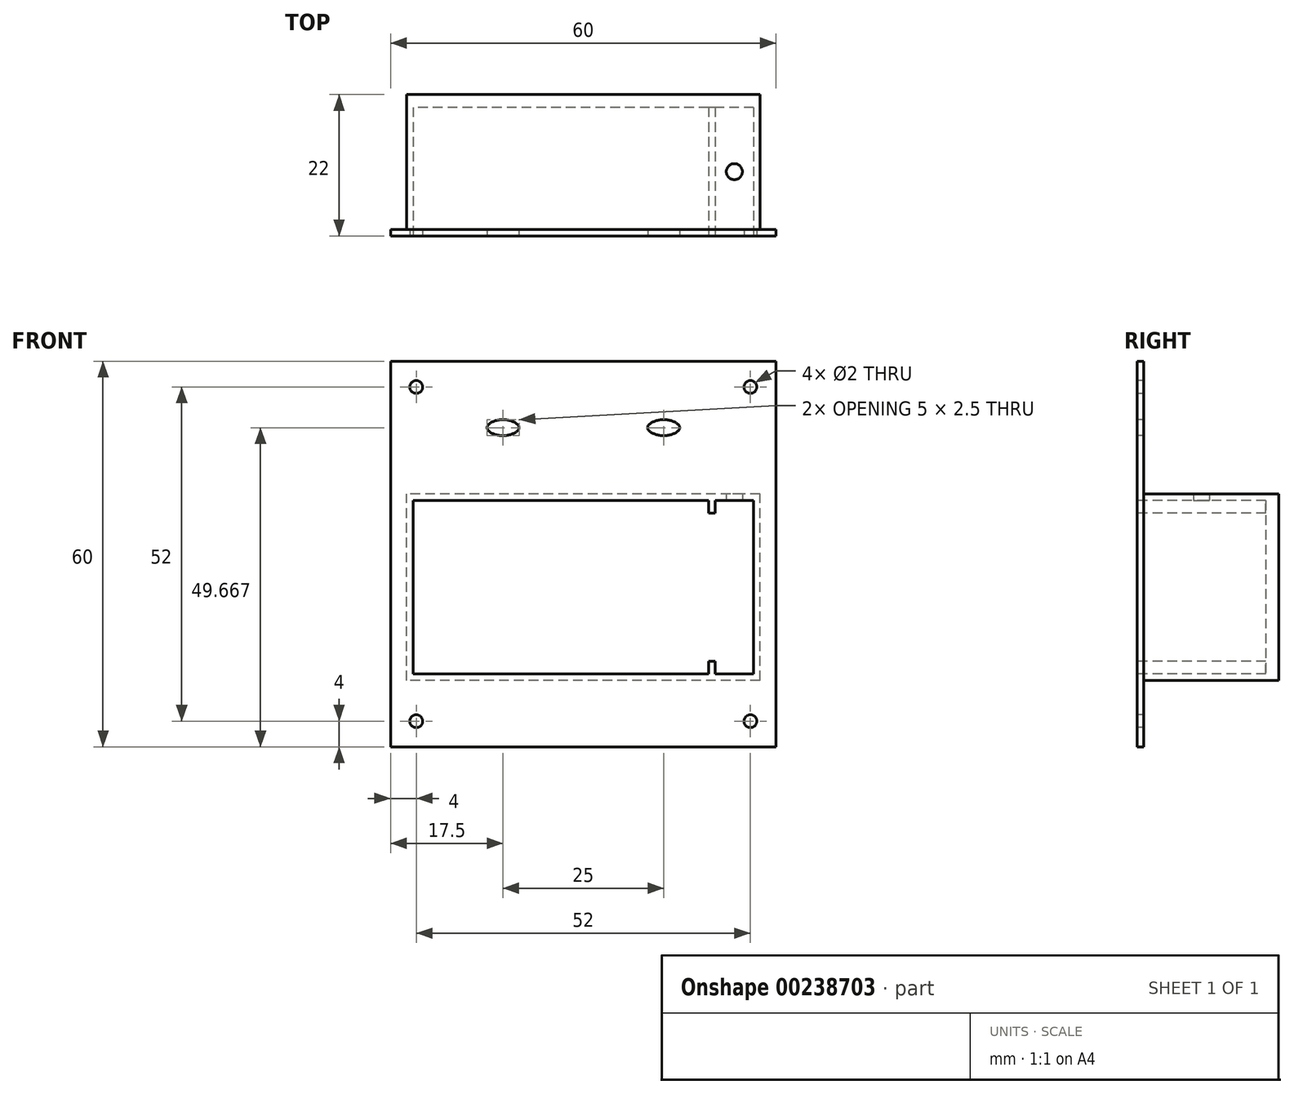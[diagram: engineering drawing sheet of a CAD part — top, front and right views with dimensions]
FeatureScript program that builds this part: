
annotation { "Feature Type Name" : "Feature", "Feature Type Description" : "" }
export const myFeature = defineFeature(function(context is Context, id is Id, definition is map)
    precondition{}
    {
        {
            var Q0;
            Q0=qCreatedBy(makeId("Front.planeOp"),FACE);
            var sketch = newSketch(context, id + "F0", { "sketchPlane" : qUnion([Q0])});
            skCircle(sketch, "E0", {"center": v(26.5, 16.25) * mm, "radius": 6.5 * mm, "construction": true});
            skCircle(sketch, "E1", {"center": v(45.5, 9.5) * mm, "radius": 4.5 * mm});
            skCircle(sketch, "E2", {"center": v(45.5, 9.5) * mm, "radius": 3 * mm});
            skCircle(sketch, "E3", {"center": v(45.5, 24.5) * mm, "radius": 3 * mm});
            skCircle(sketch, "E4", {"center": v(45.5, 24.5) * mm, "radius": 2.5 * mm});
            skLineSegment(sketch, "E5", {"start": v(45.5, 27.5) * mm, "end": v(45.5, 5) * mm, "construction": true});
            skPoint(sketch, "E6.positionSnap0", {"position": v(45.5, 16.25) * mm});
            skLineSegment(sketch, "E7.bottom", {"start": v(15, 32.5) * mm, "end": v(55, 32.5) * mm});
            skLineSegment(sketch, "E7.top", {"start": v(15, 0) * mm, "end": v(55, 0) * mm});
            skLineSegment(sketch, "E7.left", {"start": v(15, 32.5) * mm, "end": v(15, 0) * mm});
            skLineSegment(sketch, "E7.right", {"start": v(55, 32.5) * mm, "end": v(55, 0) * mm});
            skLineSegment(sketch, "E8", {"start": v(20.5, 22.25) * mm, "end": v(20.5, 23.75) * mm});
            skLineSegment(sketch, "E9", {"start": v(20.5, 23.75) * mm, "end": v(32.5, 23.75) * mm});
            skLineSegment(sketch, "E10", {"start": v(32.5, 23.75) * mm, "end": v(32.5, 22.25) * mm});
            skLineSegment(sketch, "E11", {"start": v(15, 16.25) * mm, "end": v(55, 16.25) * mm, "construction": true});
            skLineSegment(sketch, "E12.MirrorCS", {"start": v(32.5, 8.75) * mm, "end": v(32.5, 10.25) * mm});
            skLineSegment(sketch, "E13.MirrorCS", {"start": v(20.5, 8.75) * mm, "end": v(32.5, 8.75) * mm});
            skLineSegment(sketch, "E14.MirrorCS", {"start": v(20.5, 10.25) * mm, "end": v(20.5, 8.75) * mm});
            skLineSegment(sketch, "E15", {"start": v(50, 9.5) * mm, "end": v(55, 9.5) * mm, "construction": true});
            skLineSegment(sketch, "E16", {"start": v(41, 9.5) * mm, "end": v(41, 16.25) * mm, "construction": true});
            skLineSegment(sketch, "E17.bottom", {"start": v(32.5, 22.25) * mm, "end": v(20.5, 22.25) * mm});
            skLineSegment(sketch, "E17.top", {"start": v(32.5, 10.25) * mm, "end": v(20.5, 10.25) * mm});
            skLineSegment(sketch, "E17.left", {"start": v(32.5, 22.25) * mm, "end": v(32.5, 10.25) * mm});
            skLineSegment(sketch, "E17.right", {"start": v(20.5, 22.25) * mm, "end": v(20.5, 10.25) * mm});
            skLineSegment(sketch, "E18.bottom", {"start": v(24.5, 18.25) * mm, "end": v(28.5, 18.25) * mm});
            skLineSegment(sketch, "E18.top", {"start": v(24.5, 14.25) * mm, "end": v(28.5, 14.25) * mm});
            skLineSegment(sketch, "E18.left", {"start": v(24.5, 18.25) * mm, "end": v(24.5, 14.25) * mm});
            skLineSegment(sketch, "E18.right", {"start": v(28.5, 18.25) * mm, "end": v(28.5, 14.25) * mm});
            skLineSegment(sketch, "E19.1.0.0", {"start": v(92.5, 22.25) * mm, "end": v(80.5, 22.25) * mm});
            skCircle(sketch, "E19.1.0.1", {"center": v(105.5, 24.5) * mm, "radius": 2.5 * mm});
            skCircle(sketch, "E19.1.0.3", {"center": v(86.5, 16.25) * mm, "radius": 6.5 * mm, "construction": true});
            skLineSegment(sketch, "E19.1.0.4", {"start": v(115, 32.5) * mm, "end": v(115, 0) * mm});
            skLineSegment(sketch, "E19.1.0.5", {"start": v(75, 32.5) * mm, "end": v(115, 32.5) * mm});
            skLineSegment(sketch, "E19.1.0.6", {"start": v(84.5, 18.25) * mm, "end": v(84.5, 14.25) * mm});
            skLineSegment(sketch, "E19.1.0.7", {"start": v(84.5, 18.25) * mm, "end": v(88.5, 18.25) * mm});
            skLineSegment(sketch, "E19.1.0.8", {"start": v(92.5, 10.25) * mm, "end": v(80.5, 10.25) * mm});
            skLineSegment(sketch, "E19.1.0.9", {"start": v(80.5, 23.75) * mm, "end": v(92.5, 23.75) * mm});
            skCircle(sketch, "E19.1.0.10", {"center": v(105.5, 9.5) * mm, "radius": 4.5 * mm});
            skLineSegment(sketch, "E19.1.0.11", {"start": v(88.5, 18.25) * mm, "end": v(88.5, 14.25) * mm});
            skPoint(sketch, "E19.1.0.13", {"position": v(86.5, 16.25) * mm});
            skLineSegment(sketch, "E19.1.0.14", {"start": v(75, 32.5) * mm, "end": v(75, 0) * mm});
            skLineSegment(sketch, "E19.1.0.15", {"start": v(80.5, 8.75) * mm, "end": v(92.5, 8.75) * mm});
            skCircle(sketch, "E19.1.0.16", {"center": v(105.5, 9.5) * mm, "radius": 3 * mm});
            skCircle(sketch, "E19.1.0.17", {"center": v(105.5, 24.5) * mm, "radius": 3 * mm});
            skLineSegment(sketch, "E19.1.0.18", {"start": v(80.5, 22.25) * mm, "end": v(80.5, 10.25) * mm});
            skLineSegment(sketch, "E19.1.0.19", {"start": v(92.5, 22.25) * mm, "end": v(92.5, 10.25) * mm});
            skLineSegment(sketch, "E19.1.0.20", {"start": v(75, 0) * mm, "end": v(115, 0) * mm});
            skLineSegment(sketch, "E19.1.0.22", {"start": v(84.5, 14.25) * mm, "end": v(88.5, 14.25) * mm});
            skPoint(sketch, "E19.1.0.23", {"position": v(86.5, 16.25) * mm});
            skLineSegment(sketch, "E19.1.0.24", {"start": v(92.5, 23.75) * mm, "end": v(92.5, 22.25) * mm});
            skLineSegment(sketch, "E19.1.0.25", {"start": v(80.5, 22.25) * mm, "end": v(80.5, 23.75) * mm});
            skLineSegment(sketch, "E19.1.0.26", {"start": v(80.5, 10.25) * mm, "end": v(80.5, 8.75) * mm});
            skLineSegment(sketch, "E19.1.0.27", {"start": v(92.5, 8.75) * mm, "end": v(92.5, 10.25) * mm});
            skLineSegment(sketch, "E19.2.0.0", {"start": v(152.5, 22.25) * mm, "end": v(140.5, 22.25) * mm});
            skCircle(sketch, "E19.2.0.1", {"center": v(165.5, 24.5) * mm, "radius": 2.5 * mm});
            skCircle(sketch, "E19.2.0.3", {"center": v(146.5, 16.25) * mm, "radius": 6.5 * mm, "construction": true});
            skLineSegment(sketch, "E19.2.0.4", {"start": v(175, 32.5) * mm, "end": v(175, 0) * mm});
            skLineSegment(sketch, "E19.2.0.5", {"start": v(135, 32.5) * mm, "end": v(175, 32.5) * mm});
            skLineSegment(sketch, "E19.2.0.6", {"start": v(144.5, 18.25) * mm, "end": v(144.5, 14.25) * mm});
            skLineSegment(sketch, "E19.2.0.7", {"start": v(144.5, 18.25) * mm, "end": v(148.5, 18.25) * mm});
            skLineSegment(sketch, "E19.2.0.8", {"start": v(152.5, 10.25) * mm, "end": v(140.5, 10.25) * mm});
            skLineSegment(sketch, "E19.2.0.9", {"start": v(140.5, 23.75) * mm, "end": v(152.5, 23.75) * mm});
            skCircle(sketch, "E19.2.0.10", {"center": v(165.5, 9.5) * mm, "radius": 4.5 * mm});
            skLineSegment(sketch, "E19.2.0.11", {"start": v(148.5, 18.25) * mm, "end": v(148.5, 14.25) * mm});
            skPoint(sketch, "E19.2.0.13", {"position": v(146.5, 16.25) * mm});
            skLineSegment(sketch, "E19.2.0.14", {"start": v(135, 32.5) * mm, "end": v(135, 0) * mm});
            skLineSegment(sketch, "E19.2.0.15", {"start": v(140.5, 8.75) * mm, "end": v(152.5, 8.75) * mm});
            skCircle(sketch, "E19.2.0.16", {"center": v(165.5, 9.5) * mm, "radius": 3 * mm});
            skCircle(sketch, "E19.2.0.17", {"center": v(165.5, 24.5) * mm, "radius": 3 * mm});
            skLineSegment(sketch, "E19.2.0.18", {"start": v(140.5, 22.25) * mm, "end": v(140.5, 10.25) * mm});
            skLineSegment(sketch, "E19.2.0.19", {"start": v(152.5, 22.25) * mm, "end": v(152.5, 10.25) * mm});
            skLineSegment(sketch, "E19.2.0.20", {"start": v(135, 0) * mm, "end": v(175, 0) * mm});
            skLineSegment(sketch, "E19.2.0.22", {"start": v(144.5, 14.25) * mm, "end": v(148.5, 14.25) * mm});
            skPoint(sketch, "E19.2.0.23", {"position": v(146.5, 16.25) * mm});
            skLineSegment(sketch, "E19.2.0.24", {"start": v(152.5, 23.75) * mm, "end": v(152.5, 22.25) * mm});
            skLineSegment(sketch, "E19.2.0.25", {"start": v(140.5, 22.25) * mm, "end": v(140.5, 23.75) * mm});
            skLineSegment(sketch, "E19.2.0.26", {"start": v(140.5, 10.25) * mm, "end": v(140.5, 8.75) * mm});
            skLineSegment(sketch, "E19.2.0.27", {"start": v(152.5, 8.75) * mm, "end": v(152.5, 10.25) * mm});
            skLineSegment(sketch, "E19.3.0.0", {"start": v(212.5, 22.25) * mm, "end": v(200.5, 22.25) * mm});
            skCircle(sketch, "E19.3.0.1", {"center": v(225.5, 24.5) * mm, "radius": 2.5 * mm});
            skCircle(sketch, "E19.3.0.3", {"center": v(206.5, 16.25) * mm, "radius": 6.5 * mm, "construction": true});
            skLineSegment(sketch, "E19.3.0.4", {"start": v(235, 32.5) * mm, "end": v(235, 0) * mm});
            skLineSegment(sketch, "E19.3.0.5", {"start": v(195, 32.5) * mm, "end": v(235, 32.5) * mm});
            skLineSegment(sketch, "E19.3.0.6", {"start": v(204.5, 18.25) * mm, "end": v(204.5, 14.25) * mm});
            skLineSegment(sketch, "E19.3.0.7", {"start": v(204.5, 18.25) * mm, "end": v(208.5, 18.25) * mm});
            skLineSegment(sketch, "E19.3.0.8", {"start": v(212.5, 10.25) * mm, "end": v(200.5, 10.25) * mm});
            skLineSegment(sketch, "E19.3.0.9", {"start": v(200.5, 23.75) * mm, "end": v(212.5, 23.75) * mm});
            skCircle(sketch, "E19.3.0.10", {"center": v(225.5, 9.5) * mm, "radius": 4.5 * mm});
            skLineSegment(sketch, "E19.3.0.11", {"start": v(208.5, 18.25) * mm, "end": v(208.5, 14.25) * mm});
            skPoint(sketch, "E19.3.0.13", {"position": v(206.5, 16.25) * mm});
            skLineSegment(sketch, "E19.3.0.14", {"start": v(195, 32.5) * mm, "end": v(195, 0) * mm});
            skLineSegment(sketch, "E19.3.0.15", {"start": v(200.5, 8.75) * mm, "end": v(212.5, 8.75) * mm});
            skCircle(sketch, "E19.3.0.16", {"center": v(225.5, 9.5) * mm, "radius": 3 * mm});
            skCircle(sketch, "E19.3.0.17", {"center": v(225.5, 24.5) * mm, "radius": 3 * mm});
            skLineSegment(sketch, "E19.3.0.18", {"start": v(200.5, 22.25) * mm, "end": v(200.5, 10.25) * mm});
            skLineSegment(sketch, "E19.3.0.19", {"start": v(212.5, 22.25) * mm, "end": v(212.5, 10.25) * mm});
            skLineSegment(sketch, "E19.3.0.20", {"start": v(195, 0) * mm, "end": v(235, 0) * mm});
            skLineSegment(sketch, "E19.3.0.22", {"start": v(204.5, 14.25) * mm, "end": v(208.5, 14.25) * mm});
            skPoint(sketch, "E19.3.0.23", {"position": v(206.5, 16.25) * mm});
            skLineSegment(sketch, "E19.3.0.24", {"start": v(212.5, 23.75) * mm, "end": v(212.5, 22.25) * mm});
            skLineSegment(sketch, "E19.3.0.25", {"start": v(200.5, 22.25) * mm, "end": v(200.5, 23.75) * mm});
            skLineSegment(sketch, "E19.3.0.26", {"start": v(200.5, 10.25) * mm, "end": v(200.5, 8.75) * mm});
            skLineSegment(sketch, "E19.3.0.27", {"start": v(212.5, 8.75) * mm, "end": v(212.5, 10.25) * mm});
            skLineSegment(sketch, "E19.direction1", {"start": v(15, 0) * mm, "end": v(75, 0) * mm, "construction": true});
            skLineSegment(sketch, "E20.bottom", {"start": v(0, -92.5) * mm, "end": v(250, -92.5) * mm, "construction": true});
            skLineSegment(sketch, "E20.top", {"start": v(0, 47.5) * mm, "end": v(250, 47.5) * mm, "construction": true});
            skLineSegment(sketch, "E20.right", {"start": v(250, -92.5) * mm, "end": v(250, 47.5) * mm, "construction": true});
            skLineSegment(sketch, "E21", {"start": v(115, 0) * mm, "end": v(135, 0) * mm, "construction": true});
            skLineSegment(sketch, "E22.bottom", {"start": v(144.5, -39.17) * mm, "end": v(98.5, -39.17) * mm});
            skLineSegment(sketch, "E22.top", {"start": v(144.5, -66.17) * mm, "end": v(98.5, -66.17) * mm});
            skLineSegment(sketch, "E22.right", {"start": v(98.5, -39.17) * mm, "end": v(98.5, -66.17) * mm});
            skLineSegment(sketch, "E23.bottom", {"start": v(151.5, -39.17) * mm, "end": v(145.5, -39.17) * mm});
            skLineSegment(sketch, "E23.top", {"start": v(151.5, -66.17) * mm, "end": v(145.5, -66.17) * mm});
            skLineSegment(sketch, "E23.left", {"start": v(151.5, -39.17) * mm, "end": v(151.5, -66.17) * mm});
            skLineSegment(sketch, "E24.bottom", {"start": v(152.5, -67.17) * mm, "end": v(97.5, -67.17) * mm});
            skLineSegment(sketch, "E24.top", {"start": v(152.5, -38.17) * mm, "end": v(97.5, -38.17) * mm});
            skLineSegment(sketch, "E24.left", {"start": v(152.5, -67.17) * mm, "end": v(152.5, -38.17) * mm});
            skLineSegment(sketch, "E24.right", {"start": v(97.5, -67.17) * mm, "end": v(97.5, -38.17) * mm});
            skLineSegment(sketch, "E25", {"start": v(145.5, -64.17) * mm, "end": v(144.5, -64.17) * mm});
            skLineSegment(sketch, "E26", {"start": v(145.5, -41.17) * mm, "end": v(144.5, -41.17) * mm});
            skLineSegment(sketch, "E27", {"start": v(145.5, -66.17) * mm, "end": v(145.5, -64.17) * mm});
            skLineSegment(sketch, "E28", {"start": v(144.5, -66.17) * mm, "end": v(144.5, -64.17) * mm});
            skLineSegment(sketch, "E29", {"start": v(145.5, -41.17) * mm, "end": v(145.5, -39.17) * mm});
            skLineSegment(sketch, "E30", {"start": v(144.5, -41.17) * mm, "end": v(144.5, -39.17) * mm});
            skLineSegment(sketch, "E31.bottom", {"start": v(95, -77.5) * mm, "end": v(95, -17.5) * mm});
            skLineSegment(sketch, "E31.top", {"start": v(155, -77.5) * mm, "end": v(155, -17.5) * mm});
            skLineSegment(sketch, "E31.left", {"start": v(95, -77.5) * mm, "end": v(155, -77.5) * mm});
            skLineSegment(sketch, "E31.right", {"start": v(95, -17.5) * mm, "end": v(155, -17.5) * mm});
            skLineSegment(sketch, "E32", {"start": v(125, -38.17) * mm, "end": v(125, -17.5) * mm, "construction": true});
            skLineSegment(sketch, "E33", {"start": v(97.5, -67.17) * mm, "end": v(97.5, -77.5) * mm, "construction": true});
            skLineSegment(sketch, "E34", {"start": v(125, 0) * mm, "end": v(125, -92.5) * mm, "construction": true});
            skLineSegment(sketch, "E35.1.0.0", {"start": v(175, -77.5) * mm, "end": v(175, -17.5) * mm});
            skLineSegment(sketch, "E35.1.0.1", {"start": v(235, -77.5) * mm, "end": v(235, -17.5) * mm});
            skLineSegment(sketch, "E35.1.0.2", {"start": v(232.5, -67.17) * mm, "end": v(177.5, -67.17) * mm});
            skLineSegment(sketch, "E35.1.0.3", {"start": v(232.5, -67.17) * mm, "end": v(232.5, -38.17) * mm});
            skLineSegment(sketch, "E35.1.0.4", {"start": v(175, -17.5) * mm, "end": v(235, -17.5) * mm});
            skLineSegment(sketch, "E35.1.0.5", {"start": v(178.5, -39.17) * mm, "end": v(178.5, -66.17) * mm});
            skLineSegment(sketch, "E35.1.0.9", {"start": v(224.5, -66.17) * mm, "end": v(178.5, -66.17) * mm});
            skLineSegment(sketch, "E35.1.0.10", {"start": v(205, -38.17) * mm, "end": v(205, -17.5) * mm, "construction": true});
            skLineSegment(sketch, "E35.1.0.11", {"start": v(177.5, -67.17) * mm, "end": v(177.5, -77.5) * mm, "construction": true});
            skLineSegment(sketch, "E35.1.0.12", {"start": v(232.5, -38.17) * mm, "end": v(177.5, -38.17) * mm});
            skLineSegment(sketch, "E35.1.0.14", {"start": v(224.5, -39.17) * mm, "end": v(178.5, -39.17) * mm});
            skLineSegment(sketch, "E35.1.0.17", {"start": v(175, -77.5) * mm, "end": v(235, -77.5) * mm});
            skLineSegment(sketch, "E35.1.0.18", {"start": v(231.5, -39.17) * mm, "end": v(231.5, -66.17) * mm});
            skLineSegment(sketch, "E35.1.0.19", {"start": v(177.5, -67.17) * mm, "end": v(177.5, -38.17) * mm});
            skLineSegment(sketch, "E35.1.0.23", {"start": v(224.5, -41.17) * mm, "end": v(224.5, -39.17) * mm});
            skLineSegment(sketch, "E35.1.0.24", {"start": v(231.5, -39.17) * mm, "end": v(225.5, -39.17) * mm});
            skLineSegment(sketch, "E35.1.0.25", {"start": v(225.5, -41.17) * mm, "end": v(225.5, -39.17) * mm});
            skLineSegment(sketch, "E35.1.0.26", {"start": v(231.5, -66.17) * mm, "end": v(225.5, -66.17) * mm});
            skLineSegment(sketch, "E35.1.0.27", {"start": v(225.5, -66.17) * mm, "end": v(225.5, -64.17) * mm});
            skLineSegment(sketch, "E35.1.0.28", {"start": v(225.5, -41.17) * mm, "end": v(224.5, -41.17) * mm});
            skLineSegment(sketch, "E35.1.0.29", {"start": v(224.5, -66.17) * mm, "end": v(224.5, -64.17) * mm});
            skLineSegment(sketch, "E35.1.0.30", {"start": v(225.5, -64.17) * mm, "end": v(224.5, -64.17) * mm});
            skLineSegment(sketch, "E35.direction1", {"start": v(95, -77.5) * mm, "end": v(175, -77.5) * mm, "construction": true});
            skLineSegment(sketch, "E36.bottom", {"start": v(36.67, -28) * mm, "end": v(36.67, -74) * mm});
            skLineSegment(sketch, "E36.top", {"start": v(63.67, -28) * mm, "end": v(63.67, -74) * mm});
            skLineSegment(sketch, "E36.right", {"start": v(36.67, -74) * mm, "end": v(63.67, -74) * mm});
            skLineSegment(sketch, "E37.bottom", {"start": v(36.67, -21) * mm, "end": v(36.67, -27) * mm});
            skLineSegment(sketch, "E37.top", {"start": v(63.67, -21) * mm, "end": v(63.67, -27) * mm});
            skLineSegment(sketch, "E37.left", {"start": v(36.67, -21) * mm, "end": v(63.67, -21) * mm});
            skLineSegment(sketch, "E38.bottom", {"start": v(64.67, -20) * mm, "end": v(64.67, -75) * mm});
            skLineSegment(sketch, "E38.top", {"start": v(35.67, -20) * mm, "end": v(35.67, -75) * mm});
            skLineSegment(sketch, "E38.left", {"start": v(64.67, -20) * mm, "end": v(35.67, -20) * mm});
            skLineSegment(sketch, "E38.right", {"start": v(64.67, -75) * mm, "end": v(35.67, -75) * mm});
            skLineSegment(sketch, "E39", {"start": v(61.67, -27) * mm, "end": v(61.67, -28) * mm});
            skLineSegment(sketch, "E40", {"start": v(38.67, -27) * mm, "end": v(38.67, -28) * mm});
            skLineSegment(sketch, "E41", {"start": v(63.67, -27) * mm, "end": v(61.67, -27) * mm});
            skLineSegment(sketch, "E42", {"start": v(63.67, -28) * mm, "end": v(61.67, -28) * mm});
            skLineSegment(sketch, "E43", {"start": v(38.67, -27) * mm, "end": v(36.67, -27) * mm});
            skLineSegment(sketch, "E44", {"start": v(38.67, -28) * mm, "end": v(36.67, -28) * mm});
            skLineSegment(sketch, "E45.bottom", {"start": v(75, -77.5) * mm, "end": v(15, -77.5) * mm});
            skLineSegment(sketch, "E45.top", {"start": v(75, -17.5) * mm, "end": v(15, -17.5) * mm});
            skLineSegment(sketch, "E45.left", {"start": v(75, -77.5) * mm, "end": v(75, -17.5) * mm});
            skLineSegment(sketch, "E45.right", {"start": v(15, -77.5) * mm, "end": v(15, -17.5) * mm});
            skLineSegment(sketch, "E46", {"start": v(25.33, -29.08) * mm, "end": v(15, -29.08) * mm, "construction": true});
            skLineSegment(sketch, "E47", {"start": v(64.67, -29.08) * mm, "end": v(75, -29.08) * mm, "construction": true});
            skLineSegment(sketch, "E48", {"start": v(25.33, -29.08) * mm, "end": v(35.67, -29.08) * mm, "construction": true});
            skCircle(sketch, "E49", {"center": v(19, 28.5) * mm, "radius": 1 * mm});
            skCircle(sketch, "E50", {"center": v(51, 28.5) * mm, "radius": 1 * mm});
            skCircle(sketch, "E51", {"center": v(51, 4) * mm, "radius": 1 * mm});
            skCircle(sketch, "E52", {"center": v(19, 4) * mm, "radius": 1 * mm});
            skCircle(sketch, "E53", {"center": v(19, -21.5) * mm, "radius": 1 * mm});
            skCircle(sketch, "E54", {"center": v(71, -21.5) * mm, "radius": 1 * mm});
            skCircle(sketch, "E55", {"center": v(19, -73.5) * mm, "radius": 1 * mm});
            skCircle(sketch, "E56", {"center": v(71, -73.5) * mm, "radius": 1 * mm});
            skCircle(sketch, "E57.1.0.0", {"center": v(79, 28.5) * mm, "radius": 1 * mm});
            skCircle(sketch, "E57.1.0.1", {"center": v(79, 4) * mm, "radius": 1 * mm});
            skCircle(sketch, "E57.1.0.2", {"center": v(111, 4) * mm, "radius": 1 * mm});
            skCircle(sketch, "E57.1.0.3", {"center": v(111, 28.5) * mm, "radius": 1 * mm});
            skCircle(sketch, "E57.2.0.0", {"center": v(139, 28.5) * mm, "radius": 1 * mm});
            skCircle(sketch, "E57.2.0.1", {"center": v(139, 4) * mm, "radius": 1 * mm});
            skCircle(sketch, "E57.2.0.2", {"center": v(171, 4) * mm, "radius": 1 * mm});
            skCircle(sketch, "E57.2.0.3", {"center": v(171, 28.5) * mm, "radius": 1 * mm});
            skCircle(sketch, "E57.3.0.0", {"center": v(199, 28.5) * mm, "radius": 1 * mm});
            skCircle(sketch, "E57.3.0.1", {"center": v(199, 4) * mm, "radius": 1 * mm});
            skCircle(sketch, "E57.3.0.2", {"center": v(231, 4) * mm, "radius": 1 * mm});
            skCircle(sketch, "E57.3.0.3", {"center": v(231, 28.5) * mm, "radius": 1 * mm});
            skLineSegment(sketch, "E57.direction1", {"start": v(19, 4) * mm, "end": v(79, 4) * mm, "construction": true});
            skCircle(sketch, "E58.1.0.0", {"center": v(99, -73.5) * mm, "radius": 1 * mm});
            skCircle(sketch, "E58.1.0.1", {"center": v(151, -73.5) * mm, "radius": 1 * mm});
            skCircle(sketch, "E58.1.0.2", {"center": v(151, -21.5) * mm, "radius": 1 * mm});
            skCircle(sketch, "E58.1.0.3", {"center": v(99, -21.5) * mm, "radius": 1 * mm});
            skCircle(sketch, "E58.2.0.0", {"center": v(179, -73.5) * mm, "radius": 1 * mm});
            skCircle(sketch, "E58.2.0.1", {"center": v(231, -73.5) * mm, "radius": 1 * mm});
            skCircle(sketch, "E58.2.0.2", {"center": v(231, -21.5) * mm, "radius": 1 * mm});
            skCircle(sketch, "E58.2.0.3", {"center": v(179, -21.5) * mm, "radius": 1 * mm});
            skLineSegment(sketch, "E58.direction1", {"start": v(19, -73.5) * mm, "end": v(99, -73.5) * mm, "construction": true});
            skPoint(sketch, "E59.middle", {"position": v(25.33, -27.83) * mm});
            skLineSegment(sketch, "E60", {"start": v(15, -47.5) * mm, "end": v(35.67, -47.5) * mm, "construction": true});
            skPoint(sketch, "E61.1.0.0", {"position": v(112.5, -27.83) * mm});
            skLineSegment(sketch, "E62", {"start": v(112.5, -26.58) * mm, "end": v(112.5, -27.83) * mm, "construction": true});
            skLineSegment(sketch, "E63.bottom", {"start": v(115, -29.08) * mm, "end": v(110, -29.08) * mm, "construction": true});
            skLineSegment(sketch, "E63.top", {"start": v(115, -26.58) * mm, "end": v(110, -26.58) * mm, "construction": true});
            skLineSegment(sketch, "E63.left", {"start": v(115, -29.08) * mm, "end": v(115, -26.58) * mm, "construction": true});
            skLineSegment(sketch, "E63.right", {"start": v(110, -29.08) * mm, "end": v(110, -26.58) * mm, "construction": true});
            skFitSpline(sketch, "E64", {"points": [v(110, -27.83) * mm, v(110.5, -27.13) * mm, v(112.5, -26.58) * mm], "startDerivative": vector(0, 1.91) * mm, "endDerivative": vector(3.95, 0) * mm});
            skLineSegment(sketch, "E65", {"start": v(110, -27.83) * mm, "end": v(112.5, -27.83) * mm, "construction": true});
            skFitSpline(sketch, "E66.MirrorCS", {"points": [v(115, -27.83) * mm, v(114.5, -27.13) * mm, v(112.5, -26.58) * mm], "startDerivative": vector(0, 1.91) * mm, "endDerivative": vector(-3.95, 0) * mm});
            skFitSpline(sketch, "E67.MirrorCS", {"points": [v(110, -27.83) * mm, v(110.5, -28.53) * mm, v(112.5, -29.08) * mm], "startDerivative": vector(0, -1.91) * mm, "endDerivative": vector(3.95, 0) * mm});
            skFitSpline(sketch, "E68.MirrorCS", {"points": [v(115, -27.83) * mm, v(114.5, -28.53) * mm, v(112.5, -29.08) * mm], "startDerivative": vector(0, -1.91) * mm, "endDerivative": vector(-3.95, 0) * mm});
            skLineSegment(sketch, "E69", {"start": v(25.33, -17.5) * mm, "end": v(25.33, -27.83) * mm, "construction": true});
            skLineSegment(sketch, "E70.bottom", {"start": v(27.83, -29.08) * mm, "end": v(22.83, -29.08) * mm, "construction": true});
            skLineSegment(sketch, "E70.top", {"start": v(27.83, -26.58) * mm, "end": v(22.83, -26.58) * mm, "construction": true});
            skLineSegment(sketch, "E70.left", {"start": v(27.83, -29.08) * mm, "end": v(27.83, -26.58) * mm, "construction": true});
            skLineSegment(sketch, "E70.right", {"start": v(22.83, -29.08) * mm, "end": v(22.83, -26.58) * mm, "construction": true});
            skFitSpline(sketch, "E71", {"points": [v(22.83, -27.83) * mm, v(23.33, -27.13) * mm, v(25.33, -26.58) * mm], "startDerivative": vector(0, 1.91) * mm, "endDerivative": vector(3.95, 0) * mm});
            skLineSegment(sketch, "E72", {"start": v(22.83, -27.83) * mm, "end": v(25.33, -27.83) * mm, "construction": true});
            skFitSpline(sketch, "E73.MirrorCS", {"points": [v(27.83, -27.83) * mm, v(27.33, -27.13) * mm, v(25.33, -26.58) * mm], "startDerivative": vector(0, 1.91) * mm, "endDerivative": vector(-3.95, 0) * mm});
            skFitSpline(sketch, "E74.MirrorCS", {"points": [v(22.83, -27.83) * mm, v(23.33, -28.53) * mm, v(25.33, -29.08) * mm], "startDerivative": vector(0, -1.91) * mm, "endDerivative": vector(3.95, 0) * mm});
            skFitSpline(sketch, "E75.MirrorCS", {"points": [v(27.83, -27.83) * mm, v(27.33, -28.53) * mm, v(25.33, -29.08) * mm], "startDerivative": vector(0, -1.91) * mm, "endDerivative": vector(-3.95, 0) * mm});
            skFitSpline(sketch, "E76.MirrorCS", {"points": [v(135, -27.83) * mm, v(135.5, -27.13) * mm, v(137.5, -26.58) * mm], "startDerivative": vector(0, 1.91) * mm, "endDerivative": vector(3.95, 0) * mm});
            skFitSpline(sketch, "E77.MirrorCS", {"points": [v(135, -27.83) * mm, v(135.5, -28.53) * mm, v(137.5, -29.08) * mm], "startDerivative": vector(0, -1.91) * mm, "endDerivative": vector(3.95, 0) * mm});
            skFitSpline(sketch, "E78.MirrorCS", {"points": [v(140, -27.83) * mm, v(139.5, -28.53) * mm, v(137.5, -29.08) * mm], "startDerivative": vector(0, -1.91) * mm, "endDerivative": vector(-3.95, 0) * mm});
            skFitSpline(sketch, "E79.MirrorCS", {"points": [v(140, -27.83) * mm, v(139.5, -27.13) * mm, v(137.5, -26.58) * mm], "startDerivative": vector(0, 1.91) * mm, "endDerivative": vector(-3.95, 0) * mm});
            skPoint(sketch, "E80.MirrorP", {"position": v(137.5, -27.83) * mm});
            skFitSpline(sketch, "E81.MirrorCS", {"points": [v(27.83, -67.17) * mm, v(27.33, -66.47) * mm, v(25.33, -65.92) * mm], "startDerivative": vector(0, 1.91) * mm, "endDerivative": vector(-3.95, 0) * mm});
            skFitSpline(sketch, "E82.MirrorCS", {"points": [v(27.83, -67.17) * mm, v(27.33, -67.87) * mm, v(25.33, -68.42) * mm], "startDerivative": vector(0, -1.91) * mm, "endDerivative": vector(-3.95, 0) * mm});
            skFitSpline(sketch, "E83.MirrorCS", {"points": [v(22.83, -67.17) * mm, v(23.33, -67.87) * mm, v(25.33, -68.42) * mm], "startDerivative": vector(0, -1.91) * mm, "endDerivative": vector(3.95, 0) * mm});
            skFitSpline(sketch, "E84.MirrorCS", {"points": [v(22.83, -67.17) * mm, v(23.33, -66.47) * mm, v(25.33, -65.92) * mm], "startDerivative": vector(0, 1.91) * mm, "endDerivative": vector(3.95, 0) * mm});
            skPoint(sketch, "E85.1.0.0", {"position": v(192.5, -27.83) * mm});
            skLineSegment(sketch, "E86", {"start": v(192.5, -26.58) * mm, "end": v(192.5, -27.83) * mm, "construction": true});
            skLineSegment(sketch, "E87.bottom", {"start": v(195, -29.08) * mm, "end": v(190, -29.08) * mm, "construction": true});
            skLineSegment(sketch, "E87.top", {"start": v(195, -26.58) * mm, "end": v(190, -26.58) * mm, "construction": true});
            skLineSegment(sketch, "E87.left", {"start": v(195, -29.08) * mm, "end": v(195, -26.58) * mm, "construction": true});
            skLineSegment(sketch, "E87.right", {"start": v(190, -29.08) * mm, "end": v(190, -26.58) * mm, "construction": true});
            skFitSpline(sketch, "E88", {"points": [v(190, -27.83) * mm, v(190.5, -27.13) * mm, v(192.5, -26.58) * mm], "startDerivative": vector(0, 1.91) * mm, "endDerivative": vector(3.95, 0) * mm});
            skLineSegment(sketch, "E89", {"start": v(190, -27.83) * mm, "end": v(192.5, -27.83) * mm, "construction": true});
            skFitSpline(sketch, "E90.MirrorCS", {"points": [v(195, -27.83) * mm, v(194.5, -27.13) * mm, v(192.5, -26.58) * mm], "startDerivative": vector(0, 1.91) * mm, "endDerivative": vector(-3.95, 0) * mm});
            skFitSpline(sketch, "E91.MirrorCS", {"points": [v(190, -27.83) * mm, v(190.5, -28.53) * mm, v(192.5, -29.08) * mm], "startDerivative": vector(0, -1.91) * mm, "endDerivative": vector(3.95, 0) * mm});
            skFitSpline(sketch, "E92.MirrorCS", {"points": [v(195, -27.83) * mm, v(194.5, -28.53) * mm, v(192.5, -29.08) * mm], "startDerivative": vector(0, -1.91) * mm, "endDerivative": vector(-3.95, 0) * mm});
            skFitSpline(sketch, "E93.MirrorCS", {"points": [v(215, -27.83) * mm, v(215.5, -27.13) * mm, v(217.5, -26.58) * mm], "startDerivative": vector(0, 1.91) * mm, "endDerivative": vector(3.95, 0) * mm});
            skFitSpline(sketch, "E94.MirrorCS", {"points": [v(220, -27.83) * mm, v(219.5, -27.13) * mm, v(217.5, -26.58) * mm], "startDerivative": vector(0, 1.91) * mm, "endDerivative": vector(-3.95, 0) * mm});
            skFitSpline(sketch, "E95.MirrorCS", {"points": [v(220, -27.83) * mm, v(219.5, -28.53) * mm, v(217.5, -29.08) * mm], "startDerivative": vector(0, -1.91) * mm, "endDerivative": vector(-3.95, 0) * mm});
            skFitSpline(sketch, "E96.MirrorCS", {"points": [v(215, -27.83) * mm, v(215.5, -28.53) * mm, v(217.5, -29.08) * mm], "startDerivative": vector(0, -1.91) * mm, "endDerivative": vector(3.95, 0) * mm});
            skPoint(sketch, "E97.MirrorP", {"position": v(217.5, -27.83) * mm});
            skFitSpline(sketch, "E98.0", {"points": [v(28.33, -67.17) * mm, v(28.33, -67.33) * mm, v(28.25, -67.64) * mm, v(28, -67.98) * mm, v(27.67, -68.26) * mm, v(27.3, -68.48) * mm, v(26.86, -68.67) * mm, v(26.23, -68.85) * mm, v(25.7, -68.92) * mm, v(25.33, -68.92) * mm]});
            skFitSpline(sketch, "E98.1", {"points": [v(28.33, -67.17) * mm, v(28.33, -67) * mm, v(28.25, -66.7) * mm, v(28, -66.35) * mm, v(27.67, -66.08) * mm, v(27.3, -65.85) * mm, v(26.86, -65.67) * mm, v(26.23, -65.48) * mm, v(25.7, -65.42) * mm, v(25.33, -65.42) * mm]});
            skFitSpline(sketch, "E98.2", {"points": [v(22.33, -67.17) * mm, v(22.33, -67) * mm, v(22.42, -66.7) * mm, v(22.67, -66.35) * mm, v(23, -66.08) * mm, v(23.37, -65.85) * mm, v(23.8, -65.67) * mm, v(24.43, -65.48) * mm, v(24.97, -65.42) * mm, v(25.33, -65.42) * mm]});
            skFitSpline(sketch, "E98.3", {"points": [v(22.33, -67.17) * mm, v(22.33, -67.33) * mm, v(22.42, -67.64) * mm, v(22.67, -67.98) * mm, v(23, -68.26) * mm, v(23.37, -68.48) * mm, v(23.8, -68.67) * mm, v(24.43, -68.85) * mm, v(24.97, -68.92) * mm, v(25.33, -68.92) * mm]});
            skFitSpline(sketch, "E99.0", {"points": [v(28.33, -27.83) * mm, v(28.33, -28) * mm, v(28.25, -28.3) * mm, v(28, -28.65) * mm, v(27.67, -28.92) * mm, v(27.3, -29.15) * mm, v(26.86, -29.33) * mm, v(26.23, -29.52) * mm, v(25.7, -29.58) * mm, v(25.33, -29.58) * mm]});
            skFitSpline(sketch, "E99.1", {"points": [v(28.33, -27.83) * mm, v(28.33, -27.67) * mm, v(28.25, -27.36) * mm, v(28, -27.02) * mm, v(27.67, -26.74) * mm, v(27.3, -26.52) * mm, v(26.86, -26.33) * mm, v(26.23, -26.15) * mm, v(25.7, -26.08) * mm, v(25.33, -26.08) * mm]});
            skFitSpline(sketch, "E99.2", {"points": [v(22.33, -27.83) * mm, v(22.33, -27.67) * mm, v(22.42, -27.36) * mm, v(22.67, -27.02) * mm, v(23, -26.74) * mm, v(23.37, -26.52) * mm, v(23.8, -26.33) * mm, v(24.43, -26.15) * mm, v(24.97, -26.08) * mm, v(25.33, -26.08) * mm]});
            skFitSpline(sketch, "E99.3", {"points": [v(22.33, -27.83) * mm, v(22.33, -28) * mm, v(22.42, -28.3) * mm, v(22.67, -28.65) * mm, v(23, -28.92) * mm, v(23.37, -29.15) * mm, v(23.8, -29.33) * mm, v(24.43, -29.52) * mm, v(24.97, -29.58) * mm, v(25.33, -29.58) * mm]});
            skFitSpline(sketch, "E100.0", {"points": [v(115.5, -27.83) * mm, v(115.5, -28) * mm, v(115.42, -28.3) * mm, v(115.16, -28.65) * mm, v(114.84, -28.92) * mm, v(114.46, -29.15) * mm, v(114.03, -29.33) * mm, v(113.4, -29.52) * mm, v(112.87, -29.58) * mm, v(112.5, -29.58) * mm]});
            skFitSpline(sketch, "E100.1", {"points": [v(115.5, -27.83) * mm, v(115.5, -27.67) * mm, v(115.42, -27.36) * mm, v(115.16, -27.02) * mm, v(114.84, -26.74) * mm, v(114.46, -26.52) * mm, v(114.03, -26.33) * mm, v(113.4, -26.15) * mm, v(112.87, -26.08) * mm, v(112.5, -26.08) * mm]});
            skFitSpline(sketch, "E100.2", {"points": [v(109.5, -27.83) * mm, v(109.5, -27.67) * mm, v(109.58, -27.36) * mm, v(109.84, -27.02) * mm, v(110.16, -26.74) * mm, v(110.54, -26.52) * mm, v(110.97, -26.33) * mm, v(111.6, -26.15) * mm, v(112.13, -26.08) * mm, v(112.5, -26.08) * mm]});
            skFitSpline(sketch, "E100.3", {"points": [v(109.5, -27.83) * mm, v(109.5, -28) * mm, v(109.58, -28.3) * mm, v(109.84, -28.65) * mm, v(110.16, -28.92) * mm, v(110.54, -29.15) * mm, v(110.97, -29.33) * mm, v(111.6, -29.52) * mm, v(112.13, -29.58) * mm, v(112.5, -29.58) * mm]});
            skFitSpline(sketch, "E101.0", {"points": [v(195.5, -27.83) * mm, v(195.5, -27.67) * mm, v(195.42, -27.36) * mm, v(195.16, -27.02) * mm, v(194.84, -26.74) * mm, v(194.46, -26.52) * mm, v(194.03, -26.33) * mm, v(193.4, -26.15) * mm, v(192.87, -26.08) * mm, v(192.5, -26.08) * mm]});
            skFitSpline(sketch, "E101.1", {"points": [v(195.5, -27.83) * mm, v(195.5, -28) * mm, v(195.42, -28.3) * mm, v(195.16, -28.65) * mm, v(194.84, -28.92) * mm, v(194.46, -29.15) * mm, v(194.03, -29.33) * mm, v(193.4, -29.52) * mm, v(192.87, -29.58) * mm, v(192.5, -29.58) * mm]});
            skFitSpline(sketch, "E101.2", {"points": [v(189.5, -27.83) * mm, v(189.5, -28) * mm, v(189.58, -28.3) * mm, v(189.84, -28.65) * mm, v(190.16, -28.92) * mm, v(190.54, -29.15) * mm, v(190.97, -29.33) * mm, v(191.6, -29.52) * mm, v(192.13, -29.58) * mm, v(192.5, -29.58) * mm]});
            skFitSpline(sketch, "E101.3", {"points": [v(189.5, -27.83) * mm, v(189.5, -27.67) * mm, v(189.58, -27.36) * mm, v(189.84, -27.02) * mm, v(190.16, -26.74) * mm, v(190.54, -26.52) * mm, v(190.97, -26.33) * mm, v(191.6, -26.15) * mm, v(192.13, -26.08) * mm, v(192.5, -26.08) * mm]});
            skFitSpline(sketch, "E102.0", {"points": [v(134.5, -27.83) * mm, v(134.5, -28) * mm, v(134.58, -28.3) * mm, v(134.84, -28.65) * mm, v(135.16, -28.92) * mm, v(135.54, -29.15) * mm, v(135.97, -29.33) * mm, v(136.6, -29.52) * mm, v(137.13, -29.58) * mm, v(137.5, -29.58) * mm]});
            skFitSpline(sketch, "E102.1", {"points": [v(134.5, -27.83) * mm, v(134.5, -27.67) * mm, v(134.58, -27.36) * mm, v(134.84, -27.02) * mm, v(135.16, -26.74) * mm, v(135.54, -26.52) * mm, v(135.97, -26.33) * mm, v(136.6, -26.15) * mm, v(137.13, -26.08) * mm, v(137.5, -26.08) * mm]});
            skFitSpline(sketch, "E102.2", {"points": [v(140.5, -27.83) * mm, v(140.5, -27.67) * mm, v(140.42, -27.36) * mm, v(140.16, -27.02) * mm, v(139.84, -26.74) * mm, v(139.46, -26.52) * mm, v(139.03, -26.33) * mm, v(138.4, -26.15) * mm, v(137.87, -26.08) * mm, v(137.5, -26.08) * mm]});
            skFitSpline(sketch, "E102.3", {"points": [v(140.5, -27.83) * mm, v(140.5, -28) * mm, v(140.42, -28.3) * mm, v(140.16, -28.65) * mm, v(139.84, -28.92) * mm, v(139.46, -29.15) * mm, v(139.03, -29.33) * mm, v(138.4, -29.52) * mm, v(137.87, -29.58) * mm, v(137.5, -29.58) * mm]});
            skFitSpline(sketch, "E103.0", {"points": [v(220.5, -27.83) * mm, v(220.5, -28) * mm, v(220.42, -28.3) * mm, v(220.16, -28.65) * mm, v(219.84, -28.92) * mm, v(219.46, -29.15) * mm, v(219.03, -29.33) * mm, v(218.4, -29.52) * mm, v(217.87, -29.58) * mm, v(217.5, -29.58) * mm]});
            skFitSpline(sketch, "E103.1", {"points": [v(220.5, -27.83) * mm, v(220.5, -27.67) * mm, v(220.42, -27.36) * mm, v(220.16, -27.02) * mm, v(219.84, -26.74) * mm, v(219.46, -26.52) * mm, v(219.03, -26.33) * mm, v(218.4, -26.15) * mm, v(217.87, -26.08) * mm, v(217.5, -26.08) * mm]});
            skFitSpline(sketch, "E103.2", {"points": [v(214.5, -27.83) * mm, v(214.5, -27.67) * mm, v(214.58, -27.36) * mm, v(214.84, -27.02) * mm, v(215.16, -26.74) * mm, v(215.54, -26.52) * mm, v(215.97, -26.33) * mm, v(216.6, -26.15) * mm, v(217.13, -26.08) * mm, v(217.5, -26.08) * mm]});
            skFitSpline(sketch, "E103.3", {"points": [v(214.5, -27.83) * mm, v(214.5, -28) * mm, v(214.58, -28.3) * mm, v(214.84, -28.65) * mm, v(215.16, -28.92) * mm, v(215.54, -29.15) * mm, v(215.97, -29.33) * mm, v(216.6, -29.52) * mm, v(217.13, -29.58) * mm, v(217.5, -29.58) * mm]});
            skLineSegment(sketch, "E104.top", {"start": v(135, -102.5) * mm, "end": v(115, -102.5) * mm});
            skLineSegment(sketch, "E104.left", {"start": v(135, -92.5) * mm, "end": v(135, -102.5) * mm});
            skLineSegment(sketch, "E104.right", {"start": v(115, -92.5) * mm, "end": v(115, -102.5) * mm});
            skPoint(sketch, "E104.middle", {"position": v(125, -97.5) * mm});
            skLineSegment(sketch, "E105", {"start": v(135, -92.5) * mm, "end": v(155, -92.5) * mm});
            skLineSegment(sketch, "E106.1.0.0", {"start": v(155, -92.5) * mm, "end": v(155, -102.5) * mm});
            skLineSegment(sketch, "E106.1.0.1", {"start": v(175, -102.5) * mm, "end": v(155, -102.5) * mm});
            skLineSegment(sketch, "E106.1.0.2", {"start": v(175, -92.5) * mm, "end": v(175, -102.5) * mm});
            skLineSegment(sketch, "E106.1.0.3", {"start": v(175, -92.5) * mm, "end": v(195, -92.5) * mm});
            skLineSegment(sketch, "E106.2.0.0", {"start": v(195, -92.5) * mm, "end": v(195, -102.5) * mm});
            skLineSegment(sketch, "E106.2.0.1", {"start": v(215, -102.5) * mm, "end": v(195, -102.5) * mm});
            skLineSegment(sketch, "E106.2.0.2", {"start": v(215, -92.5) * mm, "end": v(215, -102.5) * mm});
            skLineSegment(sketch, "E106.2.0.3", {"start": v(215, -92.5) * mm, "end": v(235, -92.5) * mm});
            skLineSegment(sketch, "E106.direction1", {"start": v(115, -102.5) * mm, "end": v(155, -102.5) * mm, "construction": true});
            skLineSegment(sketch, "E107.0.3.0", {"start": v(235, -92.5) * mm, "end": v(235, -102.5) * mm});
            skLineSegment(sketch, "E108.MirrorCS", {"start": v(15, -92.5) * mm, "end": v(15, -102.5) * mm});
            skLineSegment(sketch, "E109.MirrorCS", {"start": v(35, -92.5) * mm, "end": v(35, -102.5) * mm});
            skLineSegment(sketch, "E110.MirrorCS", {"start": v(35, -102.5) * mm, "end": v(55, -102.5) * mm});
            skLineSegment(sketch, "E111.MirrorCS", {"start": v(55, -92.5) * mm, "end": v(55, -102.5) * mm});
            skLineSegment(sketch, "E112.MirrorCS", {"start": v(75, -92.5) * mm, "end": v(75, -102.5) * mm});
            skLineSegment(sketch, "E113.MirrorCS", {"start": v(75, -102.5) * mm, "end": v(95, -102.5) * mm});
            skLineSegment(sketch, "E114.MirrorCS", {"start": v(95, -92.5) * mm, "end": v(95, -102.5) * mm});
            skLineSegment(sketch, "E115.MirrorCS", {"start": v(35, -92.5) * mm, "end": v(15, -92.5) * mm});
            skLineSegment(sketch, "E116.MirrorCS", {"start": v(115, -92.5) * mm, "end": v(95, -92.5) * mm});
            skLineSegment(sketch, "E117.MirrorCS", {"start": v(75, -92.5) * mm, "end": v(55, -92.5) * mm});
            skLineSegment(sketch, "E118.bottom", {"start": v(250, -12.5) * mm, "end": v(260, -12.5) * mm});
            skLineSegment(sketch, "E118.top", {"start": v(250, -32.5) * mm, "end": v(260, -32.5) * mm});
            skLineSegment(sketch, "E118.right", {"start": v(260, -12.5) * mm, "end": v(260, -32.5) * mm});
            skPoint(sketch, "E118.middle", {"position": v(255, -22.5) * mm});
            skPoint(sketch, "E118.middle.positionSnap0", {"position": v(250, -22.5) * mm});
            skPoint(sketch, "E118.centerSnap0", {"position": v(250, -22.5) * mm});
            skLineSegment(sketch, "E119", {"start": v(250, -12.5) * mm, "end": v(250, 7.5) * mm});
            skLineSegment(sketch, "E120.0.1.0", {"start": v(250, 7.5) * mm, "end": v(260, 7.5) * mm});
            skLineSegment(sketch, "E120.0.1.1", {"start": v(260, 27.5) * mm, "end": v(260, 7.5) * mm});
            skLineSegment(sketch, "E120.0.1.2", {"start": v(250, 27.5) * mm, "end": v(260, 27.5) * mm});
            skLineSegment(sketch, "E120.0.1.3", {"start": v(250, 27.5) * mm, "end": v(250, 47.5) * mm});
            skLineSegment(sketch, "E120.0.2.0", {"start": v(250, 47.5) * mm, "end": v(260, 47.5) * mm});
            skLineSegment(sketch, "E120.direction1", {"start": v(250, -32.5) * mm, "end": v(275, -32.5) * mm, "construction": true});
            skLineSegment(sketch, "E120.direction2", {"start": v(250, -32.5) * mm, "end": v(250, 7.5) * mm, "construction": true});
            skLineSegment(sketch, "E121", {"start": v(255, -22.5) * mm, "end": v(250, -22.5) * mm, "construction": true});
            skLineSegment(sketch, "E122.MirrorCS", {"start": v(250, -32.5) * mm, "end": v(250, -52.5) * mm});
            skLineSegment(sketch, "E123.MirrorCS", {"start": v(250, -52.5) * mm, "end": v(260, -52.5) * mm});
            skLineSegment(sketch, "E124.MirrorCS", {"start": v(260, -72.5) * mm, "end": v(260, -52.5) * mm});
            skLineSegment(sketch, "E125.MirrorCS", {"start": v(250, -72.5) * mm, "end": v(260, -72.5) * mm});
            skLineSegment(sketch, "E126.MirrorCS", {"start": v(250, -72.5) * mm, "end": v(250, -92.5) * mm});
            skLineSegment(sketch, "E127.MirrorCS", {"start": v(250, -92.5) * mm, "end": v(260, -92.5) * mm});
            skLineSegment(sketch, "E128", {"start": v(235, -102.5) * mm, "end": v(260, -102.5) * mm});
            skLineSegment(sketch, "E129", {"start": v(260, -102.5) * mm, "end": v(260, -92.5) * mm});
            skLineSegment(sketch, "E130.MirrorCS", {"start": v(35, 47.5) * mm, "end": v(35, 57.5) * mm});
            skLineSegment(sketch, "E131.MirrorCS", {"start": v(115, 47.5) * mm, "end": v(115, 57.5) * mm});
            skLineSegment(sketch, "E132.MirrorCS", {"start": v(55, 47.5) * mm, "end": v(55, 57.5) * mm});
            skLineSegment(sketch, "E133.MirrorCS", {"start": v(155, 47.5) * mm, "end": v(155, 57.5) * mm});
            skLineSegment(sketch, "E134.MirrorCS", {"start": v(75, 47.5) * mm, "end": v(75, 57.5) * mm});
            skLineSegment(sketch, "E135.MirrorCS", {"start": v(235, 47.5) * mm, "end": v(235, 57.5) * mm});
            skLineSegment(sketch, "E136.MirrorCS", {"start": v(95, 47.5) * mm, "end": v(95, 57.5) * mm});
            skLineSegment(sketch, "E137.MirrorCS", {"start": v(15, 47.5) * mm, "end": v(15, 57.5) * mm});
            skLineSegment(sketch, "E138.MirrorCS", {"start": v(260, 57.5) * mm, "end": v(260, 47.5) * mm});
            skLineSegment(sketch, "E139.MirrorCS", {"start": v(175, 47.5) * mm, "end": v(175, 57.5) * mm});
            skLineSegment(sketch, "E140.MirrorCS", {"start": v(195, 47.5) * mm, "end": v(195, 57.5) * mm});
            skLineSegment(sketch, "E141.MirrorCS", {"start": v(135, 47.5) * mm, "end": v(135, 57.5) * mm});
            skLineSegment(sketch, "E142.MirrorCS", {"start": v(215, 47.5) * mm, "end": v(215, 57.5) * mm});
            skLineSegment(sketch, "E143.MirrorCS", {"start": v(135, 47.5) * mm, "end": v(155, 47.5) * mm});
            skLineSegment(sketch, "E144.MirrorCS", {"start": v(215, 47.5) * mm, "end": v(235, 47.5) * mm});
            skLineSegment(sketch, "E145.MirrorCS", {"start": v(175, 47.5) * mm, "end": v(195, 47.5) * mm});
            skLineSegment(sketch, "E146.MirrorCS", {"start": v(35, 47.5) * mm, "end": v(15, 47.5) * mm});
            skLineSegment(sketch, "E147.MirrorCS", {"start": v(115, 47.5) * mm, "end": v(95, 47.5) * mm});
            skLineSegment(sketch, "E148.MirrorCS", {"start": v(75, 47.5) * mm, "end": v(55, 47.5) * mm});
            skLineSegment(sketch, "E149.MirrorCS", {"start": v(135, 57.5) * mm, "end": v(115, 57.5) * mm});
            skLineSegment(sketch, "E150.MirrorCS", {"start": v(35, 57.5) * mm, "end": v(55, 57.5) * mm});
            skLineSegment(sketch, "E151.MirrorCS", {"start": v(175, 57.5) * mm, "end": v(155, 57.5) * mm});
            skLineSegment(sketch, "E152.MirrorCS", {"start": v(215, 57.5) * mm, "end": v(195, 57.5) * mm});
            skLineSegment(sketch, "E153.MirrorCS", {"start": v(75, 57.5) * mm, "end": v(95, 57.5) * mm});
            skLineSegment(sketch, "E154.MirrorCS", {"start": v(235, 57.5) * mm, "end": v(260, 57.5) * mm});
            skLineSegment(sketch, "E155.MirrorCS", {"start": v(15, -102.5) * mm, "end": v(-10, -102.5) * mm});
            skLineSegment(sketch, "E156.MirrorCS", {"start": v(-10, -102.5) * mm, "end": v(-10, -92.5) * mm});
            skLineSegment(sketch, "E157.MirrorCS", {"start": v(0, -92.5) * mm, "end": v(-10, -92.5) * mm});
            skLineSegment(sketch, "E158.MirrorCS", {"start": v(0, -72.5) * mm, "end": v(-10, -72.5) * mm});
            skLineSegment(sketch, "E159.MirrorCS", {"start": v(-10, -72.5) * mm, "end": v(-10, -52.5) * mm});
            skLineSegment(sketch, "E160.MirrorCS", {"start": v(0, -52.5) * mm, "end": v(-10, -52.5) * mm});
            skLineSegment(sketch, "E161.MirrorCS", {"start": v(0, -92.5) * mm, "end": v(0, 47.5) * mm, "construction": true});
            skLineSegment(sketch, "E162.MirrorCS", {"start": v(-10, -12.5) * mm, "end": v(-10, -32.5) * mm});
            skLineSegment(sketch, "E163.MirrorCS", {"start": v(0, -12.5) * mm, "end": v(-10, -12.5) * mm});
            skLineSegment(sketch, "E164.MirrorCS", {"start": v(0, 7.5) * mm, "end": v(-10, 7.5) * mm});
            skLineSegment(sketch, "E165.MirrorCS", {"start": v(-10, 27.5) * mm, "end": v(-10, 7.5) * mm});
            skLineSegment(sketch, "E166.MirrorCS", {"start": v(0, 27.5) * mm, "end": v(-10, 27.5) * mm});
            skLineSegment(sketch, "E167.MirrorCS", {"start": v(0, 47.5) * mm, "end": v(-10, 47.5) * mm});
            skLineSegment(sketch, "E168.MirrorCS", {"start": v(-10, 57.5) * mm, "end": v(-10, 47.5) * mm});
            skLineSegment(sketch, "E169.MirrorCS", {"start": v(0, 27.5) * mm, "end": v(0, 47.5) * mm});
            skLineSegment(sketch, "E170.MirrorCS", {"start": v(0, -12.5) * mm, "end": v(0, 7.5) * mm});
            skLineSegment(sketch, "E171.MirrorCS", {"start": v(0, -32.5) * mm, "end": v(0, -52.5) * mm});
            skLineSegment(sketch, "E172.MirrorCS", {"start": v(0, -72.5) * mm, "end": v(0, -92.5) * mm});
            skLineSegment(sketch, "E173.MirrorCS", {"start": v(0, -32.5) * mm, "end": v(-10, -32.5) * mm});
            skLineSegment(sketch, "E174", {"start": v(-10, 57.5) * mm, "end": v(15, 57.5) * mm});
            skSolve(sketch);
        }
        {
            var Q0;
            Q0=makeQuery(id+"F0.imprint","IMPRINT",FACE,{"disambiguationData":[TD([[makeQuery(id+"F0.imprint","IMPRINT",EDGE,{"derivedFrom":sQuery(id+"F0.wireOp",EDGE,"E24.bottom")}),1.0]])]});
            var Q1;
            Q1=makeQuery(id+"F0.imprint","IMPRINT",FACE,{"disambiguationData":[TD([[makeQuery(id+"F0.imprint","IMPRINT",EDGE,{"derivedFrom":sQuery(id+"F0.wireOp",EDGE,"E64")}),1.0]])]});
            var Q2;
            Q2=makeQuery(id+"F0.imprint","IMPRINT",FACE,{"disambiguationData":[TD([[makeQuery(id+"F0.imprint","IMPRINT",EDGE,{"derivedFrom":sQuery(id+"F0.wireOp",EDGE,"E76.MirrorCS")}),1.0]])]});
            var Q3;
            Q3=makeQuery(id+"F0.imprint","IMPRINT",FACE,{"disambiguationData":[TD([[makeQuery(id+"F0.imprint","IMPRINT",EDGE,{"derivedFrom":sQuery(id+"F0.wireOp",EDGE,"E22.bottom")}),-1.0]])]});
            extrude(context, id + "F1", {"entities" : qUnion([Q0, Q1, Q2, Q3]), "oppositeDirection" : true, "depth" : 1 * mm});
        }
        {
            var Q0;
            Q0=makeQuery(id+"F0.imprint","IMPRINT",FACE,{"disambiguationData":[TD([[makeQuery(id+"F0.imprint","IMPRINT",EDGE,{"derivedFrom":sQuery(id+"F0.wireOp",EDGE,"E22.bottom")}),-1.0]])]});
            extrude(context, id + "F2", {"entities" : qUnion([Q0]), "operationType" : NewBodyOperationType.ADD, "oppositeDirection" : true, "depth" : 20 * mm});
        }
        {
            var Q0;
            Q0=makeQuery(id+"F2.opExtrude","CAP_FACE",FACE,{"disambiguationData":[OSD([sQuery(id+"F0.wireOp",EDGE,"E22.bottom"),sQuery(id+"F0.wireOp",EDGE,"E22.top"),sQuery(id+"F0.wireOp",EDGE,"E22.right"),sQuery(id+"F0.wireOp",EDGE,"E23.bottom"),sQuery(id+"F0.wireOp",EDGE,"E23.top"),sQuery(id+"F0.wireOp",EDGE,"E23.left"),sQuery(id+"F0.wireOp",EDGE,"E24.bottom"),sQuery(id+"F0.wireOp",EDGE,"E24.top"),sQuery(id+"F0.wireOp",EDGE,"E24.left"),sQuery(id+"F0.wireOp",EDGE,"E24.right"),sQuery(id+"F0.wireOp",EDGE,"E25"),sQuery(id+"F0.wireOp",EDGE,"E26"),sQuery(id+"F0.wireOp",EDGE,"E27"),sQuery(id+"F0.wireOp",EDGE,"E28"),sQuery(id+"F0.wireOp",EDGE,"E29"),sQuery(id+"F0.wireOp",EDGE,"E30")])],"isStart":false});
            var sketch = newSketch(context, id + "F3", { "sketchPlane" : qUnion([Q0])});
            skLineSegment(sketch, "E175.bottom", {"start": v(-152.5, -38.17) * mm, "end": v(-97.5, -38.17) * mm});
            skLineSegment(sketch, "E175.top", {"start": v(-152.5, -67.17) * mm, "end": v(-97.5, -67.17) * mm});
            skLineSegment(sketch, "E175.left", {"start": v(-152.5, -38.17) * mm, "end": v(-152.5, -67.17) * mm});
            skLineSegment(sketch, "E175.right", {"start": v(-97.5, -38.17) * mm, "end": v(-97.5, -67.17) * mm});
            skSolve(sketch);
        }
        {
            var Q0;
            Q0=qSketchRegion(id+"F3",true);
            extrude(context, id + "F4", {"entities" : qUnion([Q0]), "operationType" : NewBodyOperationType.ADD, "depth" : 2 * mm});
        }
        {
            var Q0;
            {var subQ0=sQuery(id+"F0.wireOp",EDGE,"E23.bottom");Q0=makeQuery(id+"F2.boolean.opBoolean","MERGE",FACE,{"derivedFrom":[makeQuery(id+"F1.opExtrude","SWEPT_FACE",FACE,{"disambiguationData":[OSD([subQ0])]}),makeQuery(id+"F2.opExtrude","SWEPT_FACE",FACE,{"disambiguationData":[OSD([subQ0])]})]});}
            var sketch = newSketch(context, id + "F5", { "sketchPlane" : qUnion([Q0])});
            skCircle(sketch, "E176", {"center": v(148.5, -10) * mm, "radius": 1.25 * mm});
            skSolve(sketch);
        }
        {
            var Q0;
            Q0 = qSketchRegion(id + "F5", true);
            extrude(context, id + "F6", {"entities" : qUnion([Q0]), "operationType" : NewBodyOperationType.REMOVE, "endBound" : BoundingType.UP_TO_NEXT, "oppositeDirection" : true, "depth" : 25 * mm});
        }
    });
